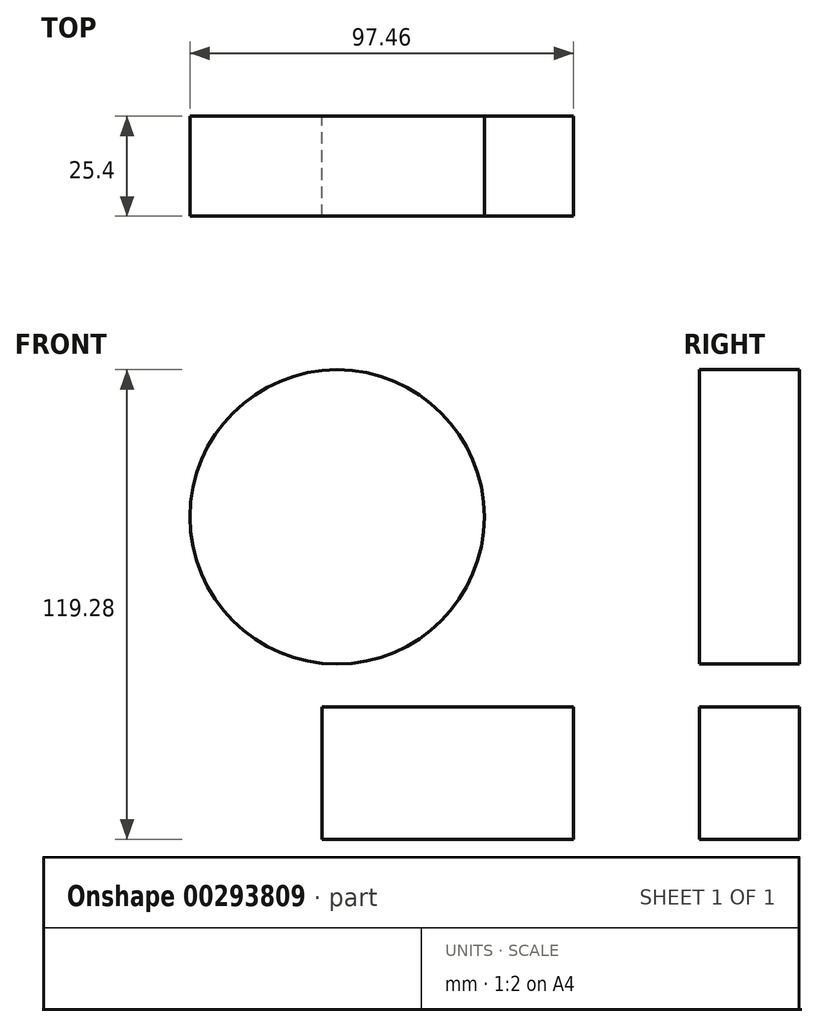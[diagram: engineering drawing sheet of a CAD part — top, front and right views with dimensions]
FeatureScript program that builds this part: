
annotation { "Feature Type Name" : "Feature", "Feature Type Description" : "" }
export const myFeature = defineFeature(function(context is Context, id is Id, definition is map)
    precondition{}
    {
        {
            var Q0;
            Q0=qCreatedBy(makeId("Front.planeOp"),FACE);
            var sketch = newSketch(context, id + "F0", { "sketchPlane" : qUnion([Q0])});
            skCircle(sketch, "E0", {"center": v(-19.94, 24.78) * mm, "radius": 37.38 * mm});
            skLineSegment(sketch, "E1.bottom", {"start": v(-23.7, -57.11) * mm, "end": v(40.14, -57.11) * mm});
            skLineSegment(sketch, "E1.top", {"start": v(-23.7, -23.44) * mm, "end": v(40.14, -23.44) * mm});
            skLineSegment(sketch, "E1.left", {"start": v(-23.7, -57.11) * mm, "end": v(-23.7, -23.44) * mm});
            skLineSegment(sketch, "E1.right", {"start": v(40.14, -57.11) * mm, "end": v(40.14, -23.44) * mm});
            skSolve(sketch);
        }
        {
            var Q0;
            Q0 = qSketchRegion(id + "F0", true);
            extrude(context, id + "F1", {"entities" : qUnion([Q0]), "depth" : 25.4 * mm});
        }
        {
            var Q0;
            Q0=makeQuery(id+"F1.opExtrude","CAP_FACE",FACE,{"disambiguationData":[OSD([sQuery(id+"F0.wireOp",EDGE,"E0")])],"isStart":false});
            var sketch = newSketch(context, id + "F2", { "sketchPlane" : qUnion([Q0])});
            skCircle(sketch, "E2", {"center": v(-41.93, 37.62) * mm, "radius": 8.28 * mm});
            skSolve(sketch);
        }
        {
            var Q0;
            Q0 = qSketchRegion(id + "F4", true);
            var Q1;
            Q1 = qSketchRegion(id + "F0", true);
            var Q2;
            Q2=sQuery(id+"F2.wireOp",EDGE,"E2");
            extrude(context, id + "F3", {"entities" : qUnion([Q0, Q1]), "operationType" : NewBodyOperationType.REMOVE, "surfaceEntities" : qUnion([Q2]), "oppositeDirection" : true, "depth" : 3683 * mm});
        }
        {
            var Q0;
            Q0=qCreatedBy(makeId("Front.planeOp"),FACE);
            var sketch = newSketch(context, id + "F4", { "sketchPlane" : qUnion([Q0])});
            skCircle(sketch, "E3", {"center": v(-10.78, 47.14) * mm, "radius": 7.45 * mm});
            skSolve(sketch);
        }
        {
            var Q0;
            Q0=makeQuery(id+"F4.imprint","IMPRINT",FACE,{"disambiguationData":[TD([[makeQuery(id+"F4.imprint","IMPRINT",EDGE,{"derivedFrom":sQuery(id+"F4.wireOp",EDGE,"E3")}),1.0]])]});
            var Q1;
            Q1 = qSketchRegion(id + "F0", true);
            extrude(context, id + "F5", {"entities" : qUnion([Q0, Q1]), "operationType" : NewBodyOperationType.REMOVE, "oppositeDirection" : true, "depth" : 3683 * mm});
        }
    });
